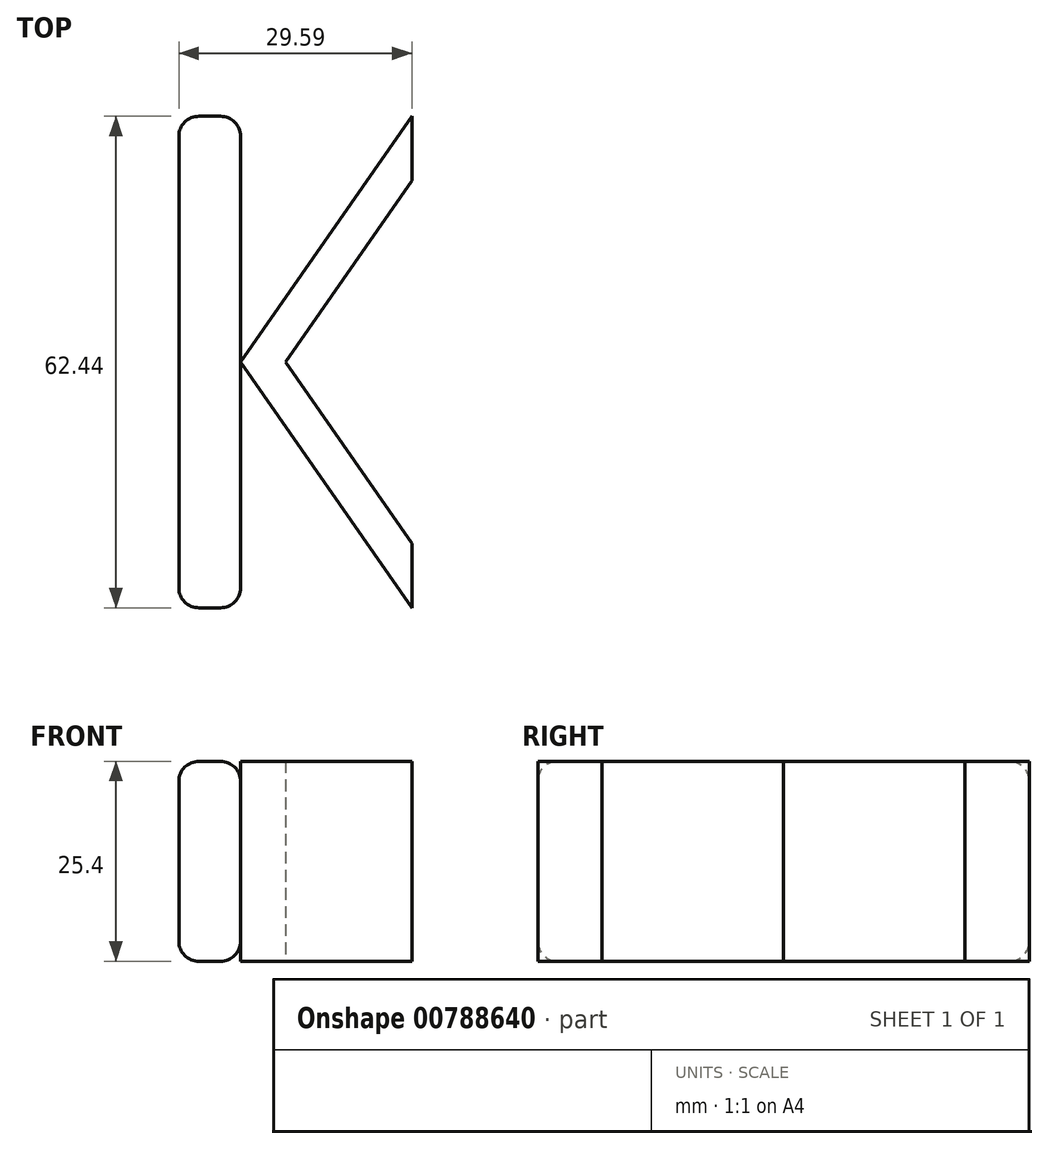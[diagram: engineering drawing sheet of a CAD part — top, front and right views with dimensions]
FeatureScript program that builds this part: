
annotation { "Feature Type Name" : "Feature", "Feature Type Description" : "" }
export const myFeature = defineFeature(function(context is Context, id is Id, definition is map)
    precondition{}
    {
        {
            var Q0;
            Q0=qCreatedBy(makeId("Top.planeOp"),FACE);
            var sketch = newSketch(context, id + "F0", { "sketchPlane" : qUnion([Q0])});
            skLineSegment(sketch, "E0.bottom", {"start": v(-26.64, 40.58) * mm, "end": v(-18.8, 40.58) * mm});
            skLineSegment(sketch, "E0.top", {"start": v(-26.64, -21.86) * mm, "end": v(-18.8, -21.86) * mm});
            skLineSegment(sketch, "E0.left", {"start": v(-26.64, 40.58) * mm, "end": v(-26.64, -21.86) * mm});
            skLineSegment(sketch, "E0.right", {"start": v(-18.8, 40.58) * mm, "end": v(-18.8, -21.86) * mm});
            skLineSegment(sketch, "E1", {"start": v(-26.64, 40.58) * mm, "end": v(-18.8, -21.86) * mm, "construction": true});
            skLineSegment(sketch, "E2", {"start": v(-26.64, -21.86) * mm, "end": v(-18.8, 40.58) * mm, "construction": true});
            skLineSegment(sketch, "E3", {"start": v(-22.72, 9.36) * mm, "end": v(-18.8, 9.36) * mm, "construction": true});
            skLineSegment(sketch, "E4", {"start": v(-18.8, 9.36) * mm, "end": v(2.95, 40.58) * mm, "construction": true});
            skLineSegment(sketch, "E5", {"start": v(2.95, 40.58) * mm, "end": v(-18.8, 9.36) * mm, "construction": true});
            skLineSegment(sketch, "E6", {"start": v(-13.1, 9.36) * mm, "end": v(2.95, 32.4) * mm, "construction": true});
            skLineSegment(sketch, "E7", {"start": v(2.95, 32.4) * mm, "end": v(-13.1, 9.36) * mm, "construction": true});
            skLineSegment(sketch, "E8", {"start": v(-13.1, 9.36) * mm, "end": v(2.95, -13.68) * mm, "construction": true});
            skLineSegment(sketch, "E9", {"start": v(2.95, -13.68) * mm, "end": v(2.95, -21.86) * mm, "construction": true});
            skLineSegment(sketch, "E10", {"start": v(2.95, 40.58) * mm, "end": v(2.95, 32.4) * mm, "construction": true});
            skLineSegment(sketch, "E11", {"start": v(-18.8, 9.36) * mm, "end": v(2.95, -21.86) * mm});
            skLineSegment(sketch, "E12", {"start": v(-18.8, 9.36) * mm, "end": v(2.95, 40.58) * mm});
            skLineSegment(sketch, "E13", {"start": v(2.95, 32.4) * mm, "end": v(2.95, 40.58) * mm});
            skLineSegment(sketch, "E14", {"start": v(2.95, 32.4) * mm, "end": v(-13.1, 9.36) * mm});
            skLineSegment(sketch, "E15", {"start": v(-13.1, 9.36) * mm, "end": v(2.95, -13.68) * mm});
            skLineSegment(sketch, "E16", {"start": v(2.95, -13.68) * mm, "end": v(2.95, -21.86) * mm});
            skSolve(sketch);
        }
        {
            var Q0;
            Q0=makeQuery(id+"F0.imprint","IMPRINT",FACE,{"disambiguationData":[TD([[makeQuery(id+"F0.imprint","IMPRINT",EDGE,{"derivedFrom":sQuery(id+"F0.wireOp",EDGE,"E11")}),1.0]])]});
            var Q1;
            {var subQ1=sQuery(id+"F0.wireOp",EDGE,"E0.bottom");Q1=makeQuery(id+"F0.imprint","IMPRINT",FACE,{"disambiguationData":[TD([[makeQuery(id+"F0.imprint","IMPRINT",EDGE,{"derivedFrom":subQ1}),-1.0]])]});}
            extrude(context, id + "F1", {"entities" : qUnion([Q0, Q1]), "depth" : 25.4 * mm, "offsetDistance" : 25.4 * mm});
        }
        {
            var Q0;
            Q0=makeQuery(id+"F1.opExtrude","SWEPT_FACE",FACE,{"disambiguationData":[OSD([sQuery(id+"F0.wireOp",EDGE,"E16")])]});
            var Q1;
            Q1=makeQuery(id+"F1.opExtrude","SWEPT_FACE",FACE,{"disambiguationData":[OSD([sQuery(id+"F0.wireOp",EDGE,"E11")])]});
            var Q2;
            Q2=makeQuery(id+"F1.opExtrude","SWEPT_EDGE",EDGE,{"disambiguationData":[OSD([sQuery(id+"F0.wireOp",EDGE,"E13"),sQuery(id+"F0.wireOp",EDGE,"E14")])]});
            var Q3;
            Q3=makeQuery(id+"F1.opExtrude","CAP_FACE",FACE,{"disambiguationData":[OSD([sQuery(id+"F0.wireOp",EDGE,"E11"),sQuery(id+"F0.wireOp",EDGE,"E12"),sQuery(id+"F0.wireOp",EDGE,"E13"),sQuery(id+"F0.wireOp",EDGE,"E14"),sQuery(id+"F0.wireOp",EDGE,"E15"),sQuery(id+"F0.wireOp",EDGE,"E16")])],"isStart":true});
            var Q4;
            Q4=makeQuery(id+"F1.opExtrude","SWEPT_EDGE",EDGE,{"disambiguationData":[OSD([sQuery(id+"F0.wireOp",EDGE,"E14"),sQuery(id+"F0.wireOp",EDGE,"E15")])]});
            var Q5;
            Q5=makeQuery(id+"F1.opExtrude","CAP_FACE",FACE,{"disambiguationData":[OSD([sQuery(id+"F0.wireOp",EDGE,"E11"),sQuery(id+"F0.wireOp",EDGE,"E12"),sQuery(id+"F0.wireOp",EDGE,"E13"),sQuery(id+"F0.wireOp",EDGE,"E14"),sQuery(id+"F0.wireOp",EDGE,"E15"),sQuery(id+"F0.wireOp",EDGE,"E16")])],"isStart":false});
            var Q6;
            Q6=makeQuery(id+"F1.opExtrude","SWEPT_FACE",FACE,{"disambiguationData":[OSD([sQuery(id+"F0.wireOp",EDGE,"E12")])]});
            var Q7;
            Q7=makeQuery(id+"F1.opExtrude","SWEPT_FACE",FACE,{"disambiguationData":[OSD([sQuery(id+"F0.wireOp",EDGE,"E13")])]});
            var Q8;
            Q8=makeQuery(id+"F1.opExtrude","SWEPT_FACE",FACE,{"disambiguationData":[OSD([sQuery(id+"F0.wireOp",EDGE,"E14")])]});
            var Q9;
            Q9=makeQuery(id+"F1.opExtrude","SWEPT_FACE",FACE,{"disambiguationData":[OSD([sQuery(id+"F0.wireOp",EDGE,"E15")])]});
            var Q10;
            Q10=makeQuery(id+"F1.opExtrude","CAP_EDGE",EDGE,{"disambiguationData":[OSD([sQuery(id+"F0.wireOp",EDGE,"E16")])],"isStart":false});
            var Q11;
            Q11=makeQuery(id+"F1.opExtrude","CAP_EDGE",EDGE,{"disambiguationData":[OSD([sQuery(id+"F0.wireOp",EDGE,"E11")])],"isStart":true});
            var Q12;
            Q12=makeQuery(id+"F1.opExtrude","CAP_EDGE",EDGE,{"disambiguationData":[OSD([sQuery(id+"F0.wireOp",EDGE,"E12")])],"isStart":true});
            var Q13;
            Q13=makeQuery(id+"F1.opExtrude","CAP_EDGE",EDGE,{"disambiguationData":[OSD([sQuery(id+"F0.wireOp",EDGE,"E14")])],"isStart":true});
            var Q14;
            Q14=makeQuery(id+"F1.opExtrude","CAP_EDGE",EDGE,{"disambiguationData":[OSD([sQuery(id+"F0.wireOp",EDGE,"E14")])],"isStart":false});
            var Q15;
            Q15=makeQuery(id+"F1.opExtrude","CAP_EDGE",EDGE,{"disambiguationData":[OSD([sQuery(id+"F0.wireOp",EDGE,"E15")])],"isStart":true});
            var Q16;
            Q16=makeQuery(id+"F1.opExtrude","CAP_EDGE",EDGE,{"disambiguationData":[OSD([sQuery(id+"F0.wireOp",EDGE,"E15")])],"isStart":false});
            var Q17;
            Q17=makeQuery(id+"F1.opExtrude","SWEPT_FACE",FACE,{"disambiguationData":[OSD([sQuery(id+"F0.wireOp",EDGE,"E0.top")])]});
            var Q18;
            Q18=makeQuery(id+"F1.opExtrude","SWEPT_FACE",FACE,{"disambiguationData":[OSD([sQuery(id+"F0.wireOp",EDGE,"E0.right")])]});
            var Q19;
            Q19=makeQuery(id+"F1.opExtrude","CAP_EDGE",EDGE,{"disambiguationData":[OSD([sQuery(id+"F0.wireOp",EDGE,"E0.right")])],"isStart":true});
            var Q20;
            Q20=makeQuery(id+"F1.opExtrude","CAP_EDGE",EDGE,{"disambiguationData":[OSD([sQuery(id+"F0.wireOp",EDGE,"E0.right")])],"isStart":false});
            var Q21;
            Q21=makeQuery(id+"F1.opExtrude","SWEPT_EDGE",EDGE,{"disambiguationData":[OSD([sQuery(id+"F0.wireOp",EDGE,"E0.right"),sQuery(id+"F0.wireOp",EDGE,"E11"),sQuery(id+"F0.wireOp",EDGE,"E12")])]});
            var Q22;
            Q22=makeQuery(id+"F1.opExtrude","SWEPT_EDGE",EDGE,{"disambiguationData":[OSD([sQuery(id+"F0.wireOp",EDGE,"E11"),sQuery(id+"F0.wireOp",EDGE,"E16")])]});
            var Q23;
            Q23=makeQuery(id+"F1.opExtrude","SWEPT_EDGE",EDGE,{"disambiguationData":[OSD([sQuery(id+"F0.wireOp",EDGE,"E12"),sQuery(id+"F0.wireOp",EDGE,"E13")])]});
            var Q24;
            Q24=makeQuery(id+"F1.opExtrude","SWEPT_EDGE",EDGE,{"disambiguationData":[OSD([sQuery(id+"F0.wireOp",EDGE,"E15"),sQuery(id+"F0.wireOp",EDGE,"E16")])]});
            var Q25;
            Q25=makeQuery(id+"F1.opExtrude","CAP_EDGE",EDGE,{"disambiguationData":[OSD([sQuery(id+"F0.wireOp",EDGE,"E11")])],"isStart":false});
            var Q26;
            Q26=makeQuery(id+"F1.opExtrude","CAP_EDGE",EDGE,{"disambiguationData":[OSD([sQuery(id+"F0.wireOp",EDGE,"E12")])],"isStart":false});
            var Q27;
            Q27=makeQuery(id+"F1.opExtrude","CAP_EDGE",EDGE,{"disambiguationData":[OSD([sQuery(id+"F0.wireOp",EDGE,"E13")])],"isStart":true});
            var Q28;
            Q28=makeQuery(id+"F1.opExtrude","CAP_EDGE",EDGE,{"disambiguationData":[OSD([sQuery(id+"F0.wireOp",EDGE,"E13")])],"isStart":false});
            var Q29;
            Q29=makeQuery(id+"F1.opExtrude","CAP_EDGE",EDGE,{"disambiguationData":[OSD([sQuery(id+"F0.wireOp",EDGE,"E16")])],"isStart":true});
            var Q30;
            Q30=makeQuery(id+"F1.opExtrude","CAP_EDGE",EDGE,{"disambiguationData":[OSD([sQuery(id+"F0.wireOp",EDGE,"E0.top")])],"isStart":false});
            var Q31;
            Q31=makeQuery(id+"F1.opExtrude","SWEPT_EDGE",EDGE,{"disambiguationData":[OSD([sQuery(id+"F0.wireOp",EDGE,"E0.bottom"),sQuery(id+"F0.wireOp",EDGE,"E0.right")])]});
            var Q32;
            Q32=makeQuery(id+"F1.opExtrude","SWEPT_EDGE",EDGE,{"disambiguationData":[OSD([sQuery(id+"F0.wireOp",EDGE,"E0.top"),sQuery(id+"F0.wireOp",EDGE,"E0.left")])]});
            var Q33;
            Q33=makeQuery(id+"F1.opExtrude","SWEPT_EDGE",EDGE,{"disambiguationData":[OSD([sQuery(id+"F0.wireOp",EDGE,"E0.top"),sQuery(id+"F0.wireOp",EDGE,"E0.right")])]});
            var Q34;
            Q34=makeQuery(id+"F1.opExtrude","CAP_EDGE",EDGE,{"disambiguationData":[OSD([sQuery(id+"F0.wireOp",EDGE,"E0.top")])],"isStart":true});
            var Q35;
            Q35=makeQuery(id+"F1.opExtrude","CAP_EDGE",EDGE,{"disambiguationData":[OSD([sQuery(id+"F0.wireOp",EDGE,"E0.left")])],"isStart":true});
            var Q36;
            Q36=makeQuery(id+"F1.opExtrude","SWEPT_FACE",FACE,{"disambiguationData":[OSD([sQuery(id+"F0.wireOp",EDGE,"E0.bottom")])]});
            var Q37;
            Q37=makeQuery(id+"F1.opExtrude","CAP_FACE",FACE,{"disambiguationData":[OSD([sQuery(id+"F0.wireOp",EDGE,"E0.bottom"),sQuery(id+"F0.wireOp",EDGE,"E0.top"),sQuery(id+"F0.wireOp",EDGE,"E0.left"),sQuery(id+"F0.wireOp",EDGE,"E0.right")])],"isStart":true});
            var Q38;
            Q38=makeQuery(id+"F1.opExtrude","CAP_FACE",FACE,{"disambiguationData":[OSD([sQuery(id+"F0.wireOp",EDGE,"E0.bottom"),sQuery(id+"F0.wireOp",EDGE,"E0.top"),sQuery(id+"F0.wireOp",EDGE,"E0.left"),sQuery(id+"F0.wireOp",EDGE,"E0.right")])],"isStart":false});
            var Q39;
            Q39=makeQuery(id+"F1.opExtrude","CAP_EDGE",EDGE,{"disambiguationData":[OSD([sQuery(id+"F0.wireOp",EDGE,"E0.bottom")])],"isStart":true});
            var Q40;
            Q40=makeQuery(id+"F1.opExtrude","CAP_EDGE",EDGE,{"disambiguationData":[OSD([sQuery(id+"F0.wireOp",EDGE,"E0.bottom")])],"isStart":false});
            var Q41;
            Q41=makeQuery(id+"F1.opExtrude","CAP_EDGE",EDGE,{"disambiguationData":[OSD([sQuery(id+"F0.wireOp",EDGE,"E0.left")])],"isStart":false});
            var Q42;
            Q42=makeQuery(id+"F1.opExtrude","SWEPT_EDGE",EDGE,{"disambiguationData":[OSD([sQuery(id+"F0.wireOp",EDGE,"E0.bottom"),sQuery(id+"F0.wireOp",EDGE,"E0.left")])]});
            var Q43;
            Q43=makeQuery(id+"F1.opExtrude","SWEPT_FACE",FACE,{"disambiguationData":[OSD([sQuery(id+"F0.wireOp",EDGE,"E0.left")])]});
            fillet(context, id + "F2", {"entities" : qUnion([Q0, Q1, Q2, Q3, Q4, Q5, Q6, Q7, Q8, Q9, Q10, Q11, Q12, Q13, Q14, Q15, Q16, Q17, Q18, Q19, Q20, Q21, Q22, Q23, Q24, Q25, Q26, Q27, Q28, Q29, Q30, Q31, Q32, Q33, Q34, Q35, Q36, Q37, Q38, Q39, Q40, Q41, Q42, Q43]), "radius" : 2.54 * mm, "tangentPropagation" : true, "allowEdgeOverflow" : false});
        }
    });
